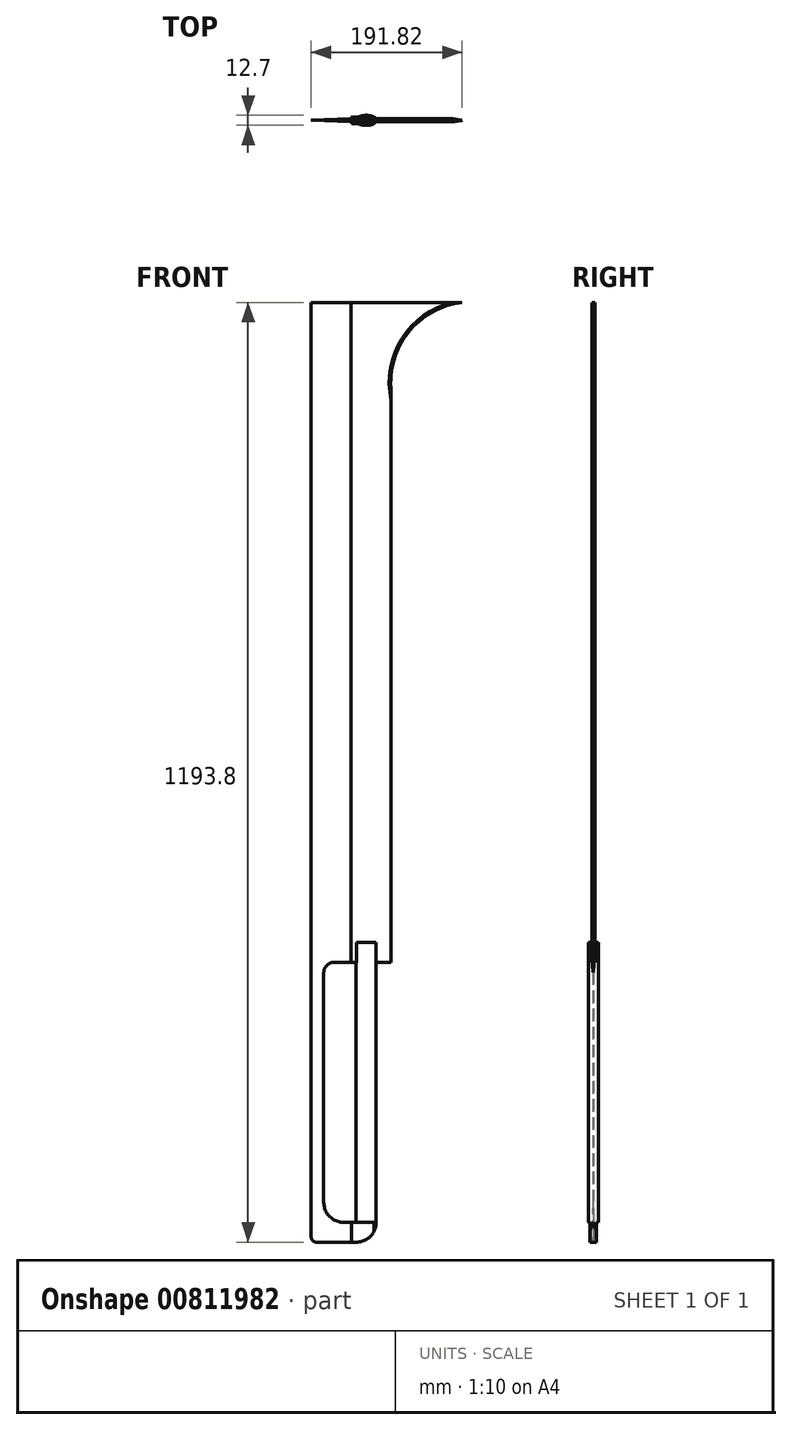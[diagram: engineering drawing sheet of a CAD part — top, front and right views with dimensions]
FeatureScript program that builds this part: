
annotation { "Feature Type Name" : "Feature", "Feature Type Description" : "" }
export const myFeature = defineFeature(function(context is Context, id is Id, definition is map)
    precondition{}
    {
        {
            var Q0;
            Q0=qCreatedBy(makeId("Front.planeOp"),FACE);
            var sketch = newSketch(context, id + "F0", { "sketchPlane" : qUnion([Q0])});
            skLineSegment(sketch, "E0", {"start": v(0, 0) * mm, "end": v(0, 838.2) * mm, "construction": true});
            skLineSegment(sketch, "E1", {"start": v(0, 0) * mm, "end": v(0, -279.4) * mm, "construction": true});
            skLineSegment(sketch, "E2", {"start": v(0, -279.4) * mm, "end": v(38.1, -279.4) * mm, "construction": true});
            skLineSegment(sketch, "E3.0", {"start": v(50.8, 0) * mm, "end": v(50.8, 838.2) * mm, "construction": true});
            skLineSegment(sketch, "E4.MirrorCS", {"start": v(-50.8, 0) * mm, "end": v(-50.8, 838.2) * mm, "construction": true});
            skLineSegment(sketch, "E5", {"start": v(50.8, 838.2) * mm, "end": v(152.4, 838.2) * mm, "construction": true});
            skLineSegment(sketch, "E6.bottom", {"start": v(-50.8, 838.2) * mm, "end": v(50.8, 838.2) * mm});
            skLineSegment(sketch, "E6.top", {"start": v(-50.8, 0) * mm, "end": v(50.8, 0) * mm});
            skLineSegment(sketch, "E6.left", {"start": v(-50.8, 838.2) * mm, "end": v(-50.8, 0) * mm});
            skLineSegment(sketch, "E6.right", {"start": v(50.8, 838.2) * mm, "end": v(50.8, 0) * mm});
            skLineSegment(sketch, "E7", {"start": v(38.1, -279.4) * mm, "end": v(38.1, 0) * mm, "construction": true});
            skSolve(sketch);
        }
        {
            var Q0;
            Q0 = qSketchRegion(id + "F0", true);
            extrude(context, id + "F1", {"entities" : qUnion([Q0]), "endBound" : BoundingType.SYMMETRIC, "depth" : 3.8 * mm, "offsetDistance" : 25.4 * mm});
        }
        {
            var Q0;
            Q0=makeQuery(id+"F1.opExtrude","SWEPT_FACE",FACE,{"disambiguationData":[OSD([sQuery(id+"F0.wireOp",EDGE,"E6.top")])]});
            var sketch = newSketch(context, id + "F2", { "sketchPlane" : qUnion([Q0])});
            skPoint(sketch, "E8.0", {"position": v(38.1, 0) * mm});
            skLineSegment(sketch, "E9", {"start": v(0, 0) * mm, "end": v(38.1, 0) * mm, "construction": true});
            skPoint(sketch, "E10", {"position": v(6.35, 0) * mm});
            skEllipse(sketch, "E11", {"center": v(19.05, 0) * mm, "majorRadius": 12.7 * mm, "minorRadius": 6.35 * mm, "majorAxis": v(-1, 0)});
            skSolve(sketch);
        }
        {
            var Q0;
            Q0 = qSketchRegion(id + "F2", true);
            extrude(context, id + "F3", {"entities" : qUnion([Q0]), "depth" : 330.2 * mm, "offsetDistance" : 25.4 * mm, "hasSecondDirection" : true, "secondDirectionOppositeDirection" : true, "secondDirectionDepth" : 25.4 * mm});
        }
        {
            var Q0;
            Q0=makeQuery(id+"F1.opExtrude","SWEPT_FACE",FACE,{"disambiguationData":[OSD([sQuery(id+"F0.wireOp",EDGE,"E6.top")])]});
            var sketch = newSketch(context, id + "F4", { "sketchPlane" : qUnion([Q0])});
            skLineSegment(sketch, "E12", {"start": v(0, 0) * mm, "end": v(-50.8, 0) * mm, "construction": true});
            skLineSegment(sketch, "E13", {"start": v(0, 1.9) * mm, "end": v(0, 25.93) * mm});
            skLineSegment(sketch, "E14", {"start": v(0, 25.93) * mm, "end": v(-64.66, 25.93) * mm});
            skLineSegment(sketch, "E15", {"start": v(-64.66, 25.93) * mm, "end": v(-64.66, -15.22) * mm});
            skLineSegment(sketch, "E16", {"start": v(-64.66, -15.22) * mm, "end": v(0, -15.22) * mm});
            skLineSegment(sketch, "E17", {"start": v(0, -15.22) * mm, "end": v(0, -1.9) * mm});
            skLineSegment(sketch, "E18", {"start": v(0, -1.9) * mm, "end": v(-50.8, 0) * mm});
            skLineSegment(sketch, "E19", {"start": v(0, 1.9) * mm, "end": v(-50.8, 0) * mm});
            skSolve(sketch);
        }
        {
            var Q0;
            Q0 = qSketchRegion(id + "F4", true);
            extrude(context, id + "F5", {"entities" : qUnion([Q0]), "operationType" : NewBodyOperationType.REMOVE, "endBound" : BoundingType.THROUGH_ALL, "oppositeDirection" : true, "depth" : 25.4 * mm, "offsetDistance" : 25.4 * mm});
        }
        {
            var Q0;
            Q0=qCreatedBy(makeId("Front.planeOp"),FACE);
            var sketch = newSketch(context, id + "F6", { "sketchPlane" : qUnion([Q0])});
            skPoint(sketch, "E20.0", {"position": v(50.8, 838.2) * mm});
            skLineSegment(sketch, "E21.0", {"start": v(50.8, 838.2) * mm, "end": v(50.8, 736.6) * mm});
            skLineSegment(sketch, "E22", {"start": v(50.8, 838.2) * mm, "end": v(152.4, 838.2) * mm});
            skArc(sketch, "E23", {"start": v(152.4, 838.2) * mm, "mid": v(80.56, 808.44) * mm, "end": v(50.8, 736.6) * mm});
            skPoint(sketch, "E24.orphan", {"position": v(50.8, -3.6) * mm});
            skSolve(sketch);
        }
        {
            var Q0;
            Q0 = qSketchRegion(id + "F6", true);
            extrude(context, id + "F7", {"entities" : qUnion([Q0]), "operationType" : NewBodyOperationType.ADD, "endBound" : BoundingType.SYMMETRIC, "depth" : 3.8 * mm, "offsetDistance" : 25.4 * mm});
        }
        {
            var Q0;
            Q0=qCreatedBy(makeId("Front.planeOp"),FACE);
            var sketch = newSketch(context, id + "F8", { "sketchPlane" : qUnion([Q0])});
            skPoint(sketch, "E25.0", {"position": v(-25.37, 16.5) * mm});
            skFitSpline(sketch, "E26.0", {"points": [v(0, 0) * mm, v(-16.93, 0) * mm, v(-33.87, 0) * mm, v(-50.8, 0) * mm]});
            skPoint(sketch, "E27.endSnap0", {"position": v(20.83, -11.36) * mm});
            skLineSegment(sketch, "E28", {"start": v(-25.37, 16.5) * mm, "end": v(-25.37, 54.6) * mm, "construction": true});
            skLineSegment(sketch, "E29", {"start": v(-114.11, 54.6) * mm, "end": v(-25.37, 54.6) * mm, "construction": true});
            skPoint(sketch, "E30", {"position": v(6.87, -184.1) * mm});
            skPoint(sketch, "E31", {"position": v(-25.37, -24.95) * mm});
            skPoint(sketch, "E32.orphan", {"position": v(6.87, -38.06) * mm});
            skPoint(sketch, "E33.orphan", {"position": v(-25.37, -117.71) * mm});
            skPoint(sketch, "E34.visualSharp", {"position": v(-29.08, -147.64) * mm});
            skPoint(sketch, "E35.visualSharp", {"position": v(-114.11, 54.6) * mm});
            skArc(sketch, "E35.filletArc", {"start": v(-132.37, 35.02) * mm, "mid": v(-135.28, 34.36) * mm, "end": v(-135.56, 31.39) * mm});
            skLineSegment(sketch, "E36", {"start": v(-34.92, -13) * mm, "end": v(-34.92, -305.08) * mm});
            skPoint(sketch, "E36.endSnap0", {"position": v(-25.7, -330.16) * mm});
            skLineSegment(sketch, "E37", {"start": v(-5.78, -330.2) * mm, "end": v(31.75, -330.2) * mm});
            skArc(sketch, "E38", {"start": v(6.35, -355.6) * mm, "mid": v(24.31, -348.16) * mm, "end": v(31.75, -330.2) * mm});
            skPoint(sketch, "E39.visualSharp", {"position": v(-34.92, -330.16) * mm});
            skArc(sketch, "E39.filletArc", {"start": v(-34.92, -305.08) * mm, "mid": v(-26.1, -324.32) * mm, "end": v(-5.78, -330.2) * mm});
            skPoint(sketch, "E40.visualSharp", {"position": v(-34.92, 0) * mm});
            skLineSegment(sketch, "E41", {"start": v(-34.92, 0) * mm, "end": v(-21.36, 0) * mm});
            skArc(sketch, "E42", {"start": v(-21.36, 0) * mm, "mid": v(-30.75, -3.78) * mm, "end": v(-34.92, -13) * mm});
            skArc(sketch, "E43.filletArc", {"start": v(-25.81, -135.03) * mm, "mid": v(-25.31, -137.34) * mm, "end": v(-24.67, -139.6) * mm});
            skLineSegment(sketch, "E44.0", {"start": v(31.75, -330.2) * mm, "end": v(6.35, -330.2) * mm, "construction": true});
            skLineSegment(sketch, "E45", {"start": v(-50.8, 0) * mm, "end": v(-50.8, -349.25) * mm});
            skLineSegment(sketch, "E46", {"start": v(-44.45, -355.6) * mm, "end": v(6.35, -355.6) * mm});
            skPoint(sketch, "E47.visualSharp", {"position": v(-50.8, -355.6) * mm});
            skArc(sketch, "E47.filletArc", {"start": v(-50.8, -349.25) * mm, "mid": v(-48.94, -353.74) * mm, "end": v(-44.45, -355.6) * mm});
            skSolve(sketch);
        }
        {
            var Q0;
            Q0 = qSketchRegion(id + "F8", true);
            extrude(context, id + "F9", {"entities" : qUnion([Q0]), "operationType" : NewBodyOperationType.ADD, "endBound" : BoundingType.SYMMETRIC, "depth" : 7.94 * mm, "offsetDistance" : 25.4 * mm});
        }
        {
            var Q0;
            Q0=makeQuery(id+"F9.opExtrude","SWEPT_FACE",FACE,{"disambiguationData":[OSD([sQuery(id+"F8.wireOp",EDGE,"E26.0")])]});
            var sketch = newSketch(context, id + "F10", { "sketchPlane" : qUnion([Q0])});
            skLineSegment(sketch, "E48", {"start": v(0, 1.9) * mm, "end": v(0, 13.25) * mm});
            skLineSegment(sketch, "E49", {"start": v(0, 13.25) * mm, "end": v(-59.97, 13.25) * mm});
            skLineSegment(sketch, "E50", {"start": v(-59.97, 13.25) * mm, "end": v(-59.97, -14.08) * mm});
            skLineSegment(sketch, "E51", {"start": v(-59.97, -14.08) * mm, "end": v(0, -14.08) * mm});
            skLineSegment(sketch, "E52", {"start": v(0, 1.9) * mm, "end": v(-50.8, 0) * mm});
            skLineSegment(sketch, "E53.0", {"start": v(-50.8, 0) * mm, "end": v(0.08, -1.9) * mm});
            skLineSegment(sketch, "E54", {"start": v(0.08, -1.9) * mm, "end": v(0, -14.08) * mm});
            skSolve(sketch);
        }
        {
            var Q0;
            Q0 = qSketchRegion(id + "F10", true);
            extrude(context, id + "F11", {"entities" : qUnion([Q0]), "operationType" : NewBodyOperationType.REMOVE, "endBound" : BoundingType.THROUGH_ALL, "oppositeDirection" : true, "depth" : 25.4 * mm, "offsetDistance" : 25.4 * mm});
        }
        {
            var Q0;
            Q0=makeQuery(id+"F9.opExtrude","SWEPT_FACE",FACE,{"disambiguationData":[OSD([sQuery(id+"F8.wireOp",EDGE,"E37")])]});
            var sketch = newSketch(context, id + "F12", { "sketchPlane" : qUnion([Q0])});
            skEllipticalArc(sketch, "E55.0", {});
            skLineSegment(sketch, "E56", {"start": v(19.05, 6.35) * mm, "end": v(19.05, 9.45) * mm});
            skLineSegment(sketch, "E57", {"start": v(19.05, 9.45) * mm, "end": v(36.49, 9.45) * mm});
            skLineSegment(sketch, "E58", {"start": v(36.49, 9.45) * mm, "end": v(36.49, -9.22) * mm});
            skLineSegment(sketch, "E59", {"start": v(36.49, -9.22) * mm, "end": v(19.05, -9.22) * mm});
            skPoint(sketch, "E59.endSnap0", {"position": v(19.05, -6.35) * mm});
            skLineSegment(sketch, "E60", {"start": v(19.05, -9.22) * mm, "end": v(19.05, -6.35) * mm});
            const initialGuessF12  = {"E55.0": [0.01905, 0, -1, 0, 0.0127, 0.00635, 1.5707963267948966, 4.71238898038469]};
            skSetInitialGuess(sketch, initialGuessF12);
            skSolve(sketch);
        }
        {
            var Q0;
            Q0 = qSketchRegion(id + "F12", true);
            extrude(context, id + "F13", {"entities" : qUnion([Q0]), "operationType" : NewBodyOperationType.REMOVE, "endBound" : BoundingType.THROUGH_ALL, "oppositeDirection" : true, "depth" : 25.4 * mm, "offsetDistance" : 25.4 * mm});
        }
        {
            var Q0;
            Q0=makeQuery(id+"F7.opExtrude","CAP_EDGE",EDGE,{"disambiguationData":[OSD([sQuery(id+"F6.wireOp",EDGE,"E23")])],"isStart":false});
            var Q1;
            Q1=makeQuery(id+"F7.opExtrude","CAP_EDGE",EDGE,{"disambiguationData":[OSD([sQuery(id+"F6.wireOp",EDGE,"E23")])],"isStart":true});
            chamfer(context, id + "F14", {"entities" : qUnion([Q0, Q1]), "width" : 2.54 * mm});
        }
    });
